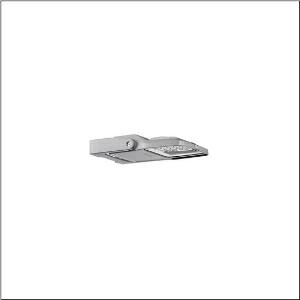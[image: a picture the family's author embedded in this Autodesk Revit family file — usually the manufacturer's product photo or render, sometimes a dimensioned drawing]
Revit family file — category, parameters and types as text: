
# Revit family: floodlight_fl_21_iq_micro___pl43_5xa7761a2a2a_4945
name_source: partatom
category: Lighting Fixtures
units: mm (PartAtom-declared; Revit-internal decimal feet)

## family parameters
Cut with Voids When Loaded = No
Host = Face
Light Source = No
Part Type = Normal
Room Calculation Point = No
Round Connector Dimension = Use Diameter
Shared = No

## types (1)
- --- (1 x LED, 3040 lm, 23.1 W, 3000K)
    Apparent Load = 23 VA
    CIE Flux Codes = 29 80 99 100 100
    Color Rendering = 70
    Color Temperature = 3000K
    Default Elevation = 1800 mm
    Description = Floodlight FL 21 iQ micro, floodlight, primary light control with lens, of PMMA, primary optical cover: protective disc, of toughened safety glass, transparent, light distribution: PL43, light emission: direct distribution, installation type: surface-mounted, lamps: LED, High Power LED, rated values: 3.040lm | 23,1W | 131,6lm/W (begin service life); end service life: 3.040lm | 23,8W; at 50% lumin. flux: 1.520lm | 11W | 138,2lm/W, colour temperature: 3000K, colour rendering: CRI > 70, light colour: 730, light setting 1 begin service life: 100% | 3.040lm | 23,1W | 131,6lm/W | 3.000K, light setting 1 end service life: 23,8W, further light settings possible, control: optimised constant luminous flux control (CLO 2.0), Desk-Remote (wireless, voltage-free reading and setting of iQ features in the workshop via application-optimized NFC function/RFID function), Light-Fading, Smart-Wire, Night-Set, Lumen-Switch, Temp-Guard, Auto-Match, pre-setting: linear dimming characteristic, with terminal, 6-pole, mains connection: 220..240V, AC, 50/60Hz, luminaire housing, of diecast aluminium, powder-coated, SITECO metallic grey (DB 702S), corrosivity category C5 mid according to DIN EN ISO 12944suitable for swimming poolschlorine-resistant, sealing non-destructively replaceable, design bracket, of diecast aluminium, powder-coated, SITECO metallic grey (DB 702S), protection rating (complete): IP66, insulation class (complete): insulation class II (safety insulation), certification: CE, ENEC, VDE, protection symbol: D, impact resistance: IK07, permissible operating ambient temperature: -40..+40°C, permissible operating ambient temperature for outdoor applications: -40..+50°C, standard: DIN EN 12944, LABS conformity tested according to VDMA 24364:2018-05, packaging unit: 1 piece

Light Distribution: PL43
    Height = 65 mm
    Lamp = 1 x LED
    Lamp Light Flux = 3040 lm
    Lamp Power = 23.1 W
    Lamp count = 1
    Length = 312 mm
    Luminous efficacy = 132 lm/W
    Manufacturer = Siteco
    ModVariant = No
    Model = 5XA7761A2A2A
    Mounting Place = Wall
    Mounting Type = Surface mounted
    Number of Poles = 1
    OnlyDefault = Yes
    Power Factor = 1
    Product Name = Floodlight FL 21 iQ micro | PL43
    Product group = floodlight | wall mounted
    ProductGroupID = 2002
    Protection Class = Protection class II
    Protection Degree = IP 66
    RLX_Detail_Level = 1
    RLX_Emergency_Light_Flux = 0 lm
    RLX_Emergency_Type = 0
    RLX_Emergency_Type_DB = No
    RlxData = <blob elided: 97645 chars, md5=72cd7de3>
    Socket = socket
    Standby Power = 0 W
    System Light Flux = 3040 lm
    System Power = 23 W
    Type Comments = factory setting: luminous flux: 100 % | dim-lin: 254 | 455 mA
    Type Image = l_1006878.jpg
    URL = http://relux.com
    VarID = @adj_177905
    Voltage = 0 V
    Weight = 0.00 kg
    Width = 230 mm

## geometry (parser evidence)
native form markers: Blend x4, Sweep x12
no freeform markers — native parametric forms only
